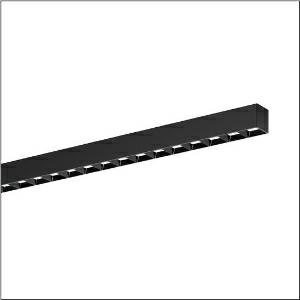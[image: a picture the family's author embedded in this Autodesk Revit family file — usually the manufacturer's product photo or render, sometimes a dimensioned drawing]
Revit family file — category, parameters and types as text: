
# Revit family: silica_21_51mx22dc3abb
name_source: partatom
category: Lighting Fixtures
units: mm (PartAtom-declared; Revit-internal decimal feet)

## family parameters
Cut with Voids When Loaded = No
Host = Face
Light Source = No
Part Type = Normal
Room Calculation Point = No
Round Connector Dimension = Use Diameter
Shared = No

## types (1)
- --- (1 x LED, 10800 lm, 69.2 W, 3000K)
    Apparent Load = 69 VA
    CIE Flux Codes = 86 100 100 100 100
    Color Rendering = 80
    Color Temperature = 3000K
    Default Elevation = 1800 mm
    Description = Silica 21, office luminaire, primary light control with darklight reflector, of PMMA, black, CAT 2 (L<= 3000cd/m²), light emission: direct distribution, primary light characteristic: symmetric, installation type: surface-mounted, LED, rated luminous flux: 10.800lm, luminous efficacy: 156lm/W, light colour: 830, colour temperature: 3000K, control gear: DALI 2, with terminal, 3+2-pole, max. 2.5mm², mains connection: 220..240V, AC, 50/60Hz, rated input power: 69.2W, luminaire housing, of aluminium, matt jet black (RAL 9005), length: 3.004mm, width: 53mm, height: 53mm, protection rating (complete): IP20, insulation class (complete): insulation class I (protective earthing), certification: CE, permissible operating ambient temperature: 0..+35°C, standard: EN 50419, packaging unit: 1 piece
    Height = 53 mm
    Lamp = 1 x LED
    Lamp Light Flux = 10800 lm
    Lamp Power = 69.2 W
    Lamp count = 1
    Length = 3004 mm
    Luminous efficacy = 156 lm/W
    Manufacturer = Siteco
    ModVariant = No
    Model = 51MX22DC3ABB
    Mounting Place = Ceiling
    Mounting Type = Surface mounted
    Number of Poles = 1
    OnlyDefault = Yes
    Power Factor = 1
    Product Name = Silica 21
    Product group = office luminaire | ceiling mounted
    ProductGroupID = 301
    Protection Class = Protection class I
    Protection Degree = IP 20
    RLX_Detail_Level = 1
    RLX_Emergency_Light_Flux = 0 lm
    RLX_Emergency_Type = 0
    RLX_Emergency_Type_DB = No
    RlxData = <blob elided: 64297 chars, md5=4f5f02d4>
    Socket = socket
    Standby Power = 0 W
    System Light Flux = 10800 lm
    System Power = 69 W
    Type Comments = factory setting: luminous flux: 100 % | dim-lin: 254 | 392 mA
    Type Image = l_1335908.jpg
    URL = http://relux.com
    VarID = @adj_124839
    Voltage = 0 V
    Weight = 0.00 kg
    Width = 53 mm

## geometry (parser evidence)
native form markers: Blend x4, Sweep x10
no freeform markers — native parametric forms only
